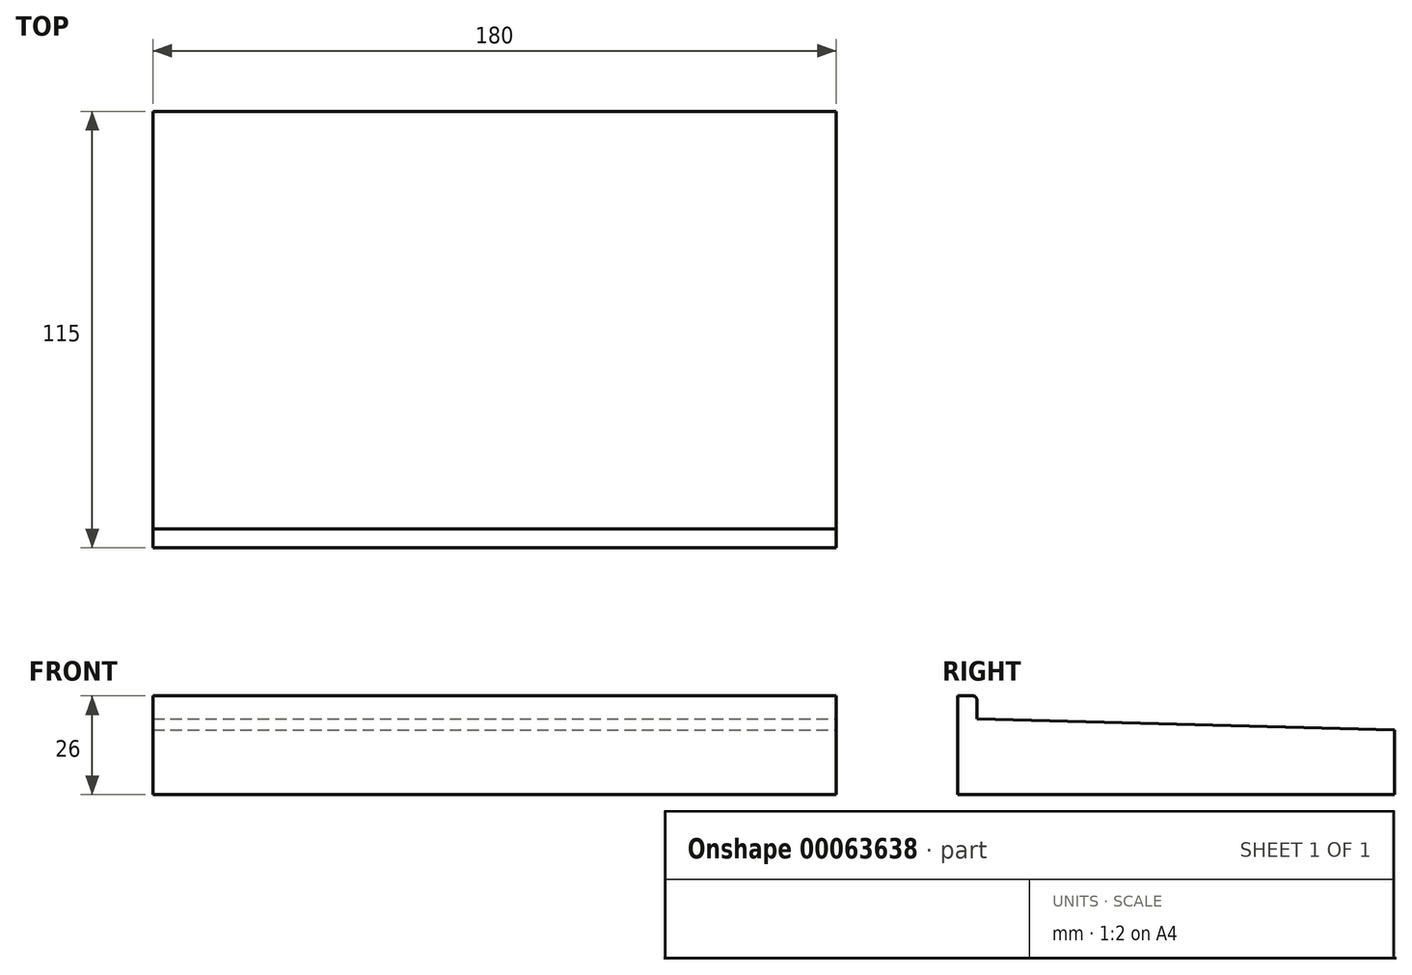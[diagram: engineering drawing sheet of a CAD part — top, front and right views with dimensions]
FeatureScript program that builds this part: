
annotation { "Feature Type Name" : "Feature", "Feature Type Description" : "" }
export const myFeature = defineFeature(function(context is Context, id is Id, definition is map)
    precondition{}
    {
        {
            var Q0;
            Q0=qCreatedBy(makeId("Right.planeOp"),FACE);
            var sketch = newSketch(context, id + "F0", { "sketchPlane" : qUnion([Q0])});
            skLineSegment(sketch, "E0", {"start": v(-4.52, 25.46) * mm, "end": v(-4.52, 5.46) * mm});
            skLineSegment(sketch, "E1", {"start": v(-4.52, 5.46) * mm, "end": v(105.48, 5.46) * mm});
            skLineSegment(sketch, "E2", {"start": v(105.48, 5.46) * mm, "end": v(105.48, 22.46) * mm});
            skLineSegment(sketch, "E3", {"start": v(-4.52, 25.46) * mm, "end": v(105.48, 22.46) * mm});
            skSolve(sketch);
        }
        {
            var Q0;
            Q0 = qSketchRegion(id + "F0", true);
            extrude(context, id + "F1", {"entities" : qUnion([Q0]), "oppositeDirection" : true, "depth" : 180 * mm});
        }
        {
            var Q0;
            Q0=makeQuery(id+"F1.opExtrude","SWEPT_FACE",FACE,{"disambiguationData":[OSD([sQuery(id+"F0.wireOp",EDGE,"E0")])]});
            var sketch = newSketch(context, id + "F2", { "sketchPlane" : qUnion([Q0])});
            skLineSegment(sketch, "E4.bottom", {"start": v(-120, 5.46) * mm, "end": v(-60, 5.46) * mm});
            skLineSegment(sketch, "E4.top", {"start": v(-120, 31.46) * mm, "end": v(-60, 31.46) * mm});
            skLineSegment(sketch, "E4.left", {"start": v(-120, 5.46) * mm, "end": v(-120, 31.46) * mm});
            skLineSegment(sketch, "E4.right", {"start": v(-60, 5.46) * mm, "end": v(-60, 31.46) * mm});
            skSolve(sketch);
        }
        {
            var Q0;
            {var subQ0=sQuery(id+"F2.wireOp",EDGE,"E4.top");Q0=makeQuery(id+"F2.imprint","IMPRINT",FACE,{"disambiguationData":[TD([[makeQuery(id+"F2.imprint","IMPRINT",EDGE,{"derivedFrom":subQ0}),-1.0]])]});}
            var Q1;
            {var subQ0=sQuery(id+"F2.wireOp",EDGE,"E4.bottom");Q1=makeQuery(id+"F2.imprint","IMPRINT",FACE,{"disambiguationData":[TD([[makeQuery(id+"F2.imprint","IMPRINT",EDGE,{"derivedFrom":subQ0}),1.0]])]});}
            extrude(context, id + "F3", {"entities" : qUnion([Q0, Q1]), "operationType" : NewBodyOperationType.ADD, "depth" : 5 * mm});
        }
        {
            var Q0;
            Q0=makeQuery(id+"F3.opExtrude","CAP_EDGE",EDGE,{"disambiguationData":[OSD([sQuery(id+"F2.wireOp",EDGE,"E4.top")])],"isStart":true});
            fillet(context, id + "F4", {"entities" : qUnion([Q0]), "radius" : 1 * mm, "tangentPropagation" : true, "allowEdgeOverflow" : false});
        }
        {
            var Q0;
            Q0=makeQuery(id+"F3.opExtrude","SWEPT_FACE",FACE,{"disambiguationData":[OSD([sQuery(id+"F2.wireOp",EDGE,"E4.right")])]});
            var Q1;
            Q1=makeQuery(id+"F1.opExtrude","CAP_FACE",FACE,{"disambiguationData":[OSD([sQuery(id+"F0.wireOp",EDGE,"E0"),sQuery(id+"F0.wireOp",EDGE,"E1"),sQuery(id+"F0.wireOp",EDGE,"E2"),sQuery(id+"F0.wireOp",EDGE,"E3")])],"isStart":true});
            extrude(context, id + "F5", {"entities" : qUnion([Q0]), "operationType" : NewBodyOperationType.ADD, "endBound" : BoundingType.UP_TO_SURFACE, "endBoundEntityFace" : qUnion([Q1]), "depth" : 25 * mm});
        }
        {
            var Q0;
            Q0=makeQuery(id+"F3.opExtrude","SWEPT_FACE",FACE,{"disambiguationData":[OSD([sQuery(id+"F2.wireOp",EDGE,"E4.left")])]});
            var Q1;
            Q1=makeQuery(id+"F1.opExtrude","CAP_FACE",FACE,{"disambiguationData":[OSD([sQuery(id+"F0.wireOp",EDGE,"E0"),sQuery(id+"F0.wireOp",EDGE,"E1"),sQuery(id+"F0.wireOp",EDGE,"E2"),sQuery(id+"F0.wireOp",EDGE,"E3")])],"isStart":false});
            extrude(context, id + "F6", {"entities" : qUnion([Q0]), "operationType" : NewBodyOperationType.ADD, "endBound" : BoundingType.UP_TO_SURFACE, "endBoundEntityFace" : qUnion([Q1]), "depth" : 25 * mm});
        }
    });
